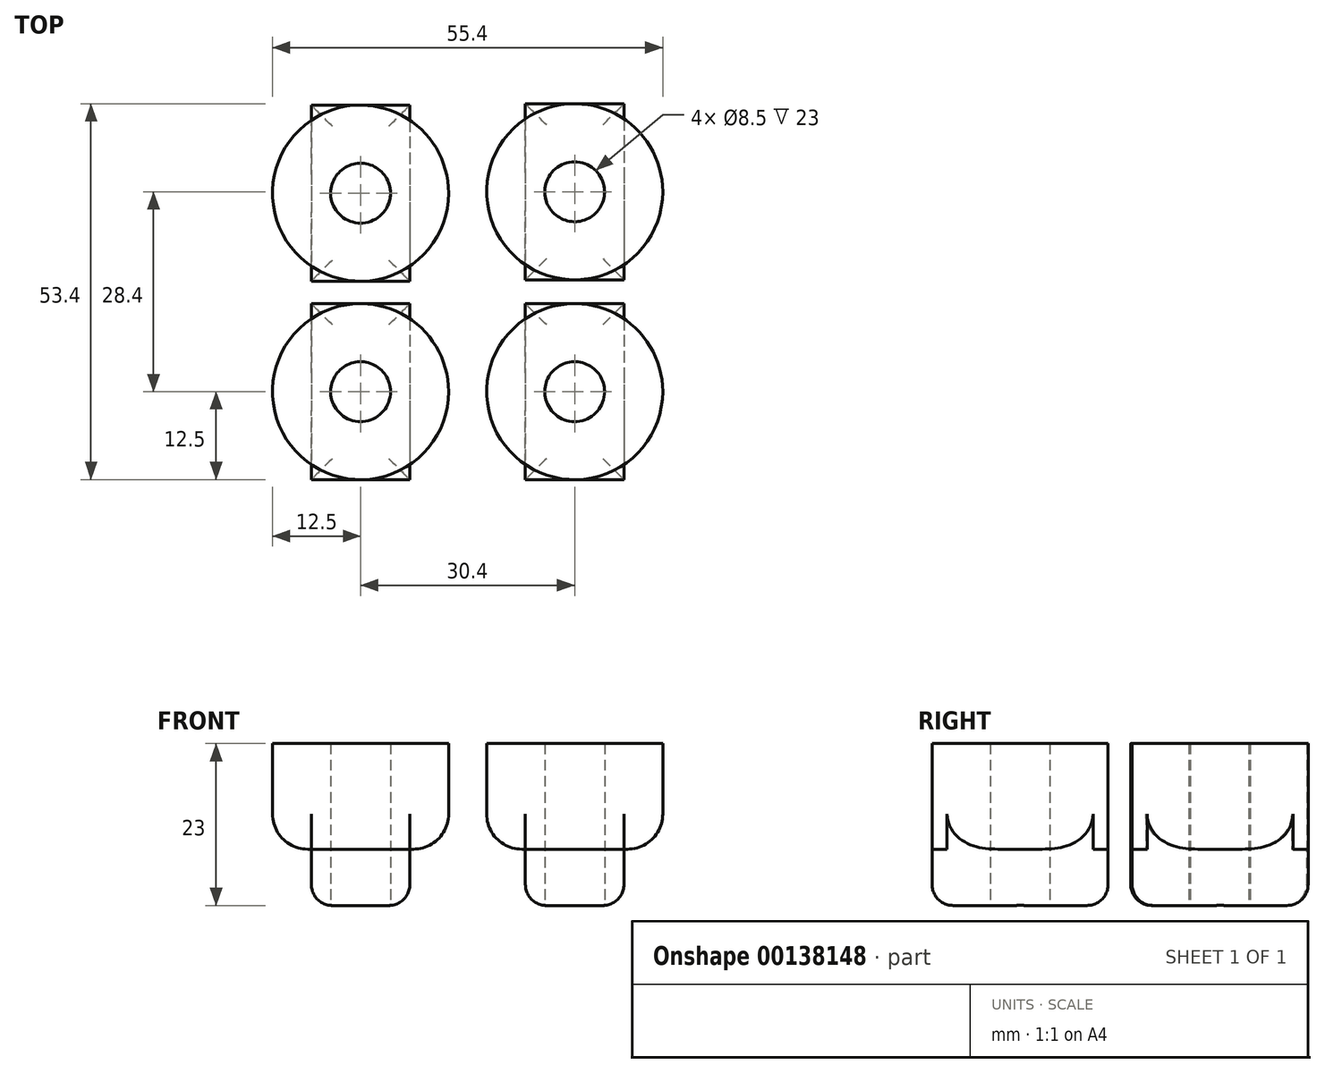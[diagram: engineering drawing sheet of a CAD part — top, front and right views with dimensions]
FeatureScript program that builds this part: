
annotation { "Feature Type Name" : "Feature", "Feature Type Description" : "" }
export const myFeature = defineFeature(function(context is Context, id is Id, definition is map)
    precondition{}
    {
        {
            var Q0;
            Q0=qCreatedBy(makeId("Top.planeOp"),FACE);
            var sketch = newSketch(context, id + "F0", { "sketchPlane" : qUnion([Q0])});
            skCircle(sketch, "E0", {"center": v(0, 0) * mm, "radius": 12.5 * mm});
            skCircle(sketch, "E1", {"center": v(0, 0) * mm, "radius": 4.25 * mm});
            skSolve(sketch);
        }
        {
            var Q0;
            Q0=makeQuery(id+"F0.imprint","IMPRINT",FACE,{"disambiguationData":[TD([[makeQuery(id+"F0.imprint","IMPRINT",EDGE,{"derivedFrom":sQuery(id+"F0.wireOp",EDGE,"E0")}),1.0]])]});
            extrude(context, id + "F1", {"entities" : qUnion([Q0]), "depth" : 15 * mm});
        }
        {
            var Q0;
            Q0=qCreatedBy(makeId("Top.planeOp"),FACE);
            var sketch = newSketch(context, id + "F2", { "sketchPlane" : qUnion([Q0])});
            skLineSegment(sketch, "E2.bottom", {"start": v(-7, 12.5) * mm, "end": v(7, 12.5) * mm});
            skLineSegment(sketch, "E2.top", {"start": v(-7, -12.5) * mm, "end": v(7, -12.5) * mm});
            skLineSegment(sketch, "E2.left", {"start": v(-7, 12.5) * mm, "end": v(-7, -12.5) * mm});
            skLineSegment(sketch, "E2.right", {"start": v(7, 12.5) * mm, "end": v(7, -12.5) * mm});
            skPoint(sketch, "E2.middle", {"position": v(0, 0) * mm});
            skSolve(sketch);
        }
        {
            var Q0;
            Q0=makeQuery(id+"F2.imprint","IMPRINT",FACE,{"disambiguationData":[TD([[makeQuery(id+"F2.imprint","IMPRINT",EDGE,{"derivedFrom":sQuery(id+"F2.wireOp",EDGE,"E2.bottom")}),-1.0]])]});
            extrude(context, id + "F3", {"entities" : qUnion([Q0]), "operationType" : NewBodyOperationType.ADD, "oppositeDirection" : true, "depth" : 8 * mm});
        }
        {
            var Q0;
            Q0=makeQuery(id+"F3.boolean.opBoolean","SPLIT",FACE,{"disambiguationData":[TD([makeQuery(id+"F1.opExtrude","SWEPT_FACE",FACE,{"disambiguationData":[OSD([sQuery(id+"F0.wireOp",EDGE,"E1")])]})])],"derivedFrom":makeQuery(id+"F3.opExtrude","CAP_FACE",FACE,{"disambiguationData":[OSD([sQuery(id+"F2.wireOp",EDGE,"E2.bottom"),sQuery(id+"F2.wireOp",EDGE,"E2.top"),sQuery(id+"F2.wireOp",EDGE,"E2.left"),sQuery(id+"F2.wireOp",EDGE,"E2.right")])],"isStart":true})});
            extrude(context, id + "F4", {"entities" : qUnion([Q0]), "operationType" : NewBodyOperationType.REMOVE, "oppositeDirection" : true, "depth" : 10 * mm});
        }
        {
            var Q0;
            Q0=makeQuery(id+"F3.opExtrude","CAP_EDGE",EDGE,{"disambiguationData":[OSD([sQuery(id+"F2.wireOp",EDGE,"E2.top")])],"isStart":false});
            var Q1;
            Q1=makeQuery(id+"F3.opExtrude","CAP_EDGE",EDGE,{"disambiguationData":[OSD([sQuery(id+"F2.wireOp",EDGE,"E2.right")])],"isStart":false});
            var Q2;
            Q2=makeQuery(id+"F3.opExtrude","CAP_EDGE",EDGE,{"disambiguationData":[OSD([sQuery(id+"F2.wireOp",EDGE,"E2.bottom")])],"isStart":false});
            var Q3;
            Q3=makeQuery(id+"F3.opExtrude","CAP_EDGE",EDGE,{"disambiguationData":[OSD([sQuery(id+"F2.wireOp",EDGE,"E2.left")])],"isStart":false});
            fillet(context, id + "F5", {"entities" : qUnion([Q0, Q1, Q2, Q3]), "radius" : 3 * mm, "tangentPropagation" : true, "allowEdgeOverflow" : false});
        }
        {
            var Q0;
            {var subQ0=sQuery(id+"F2.wireOp",EDGE,"E2.right");var subQ1=sQuery(id+"F2.wireOp",EDGE,"E2.bottom");var subQ2=makeQuery(id+"F3.opExtrude","CAP_FACE",FACE,{"disambiguationData":[OSD([subQ1,sQuery(id+"F2.wireOp",EDGE,"E2.top"),sQuery(id+"F2.wireOp",EDGE,"E2.left"),subQ0])],"isStart":true});var subQ3=sQuery(id+"F0.wireOp",EDGE,"E0");var subQ4=makeQuery(id+"F1.opExtrude","SWEPT_FACE",FACE,{"disambiguationData":[OSD([subQ3])]});Q0=makeQuery(id+"F3.boolean.opBoolean","SPLIT",EDGE,{"disambiguationData":[topologyDisambiguationEdgeConnected([subQ4,subQ2]),TD([subQ4,makeQuery(id+"F1.opExtrude","CAP_FACE",FACE,{"disambiguationData":[OSD([subQ3,sQuery(id+"F0.wireOp",EDGE,"E1")])],"isStart":true}),makeQuery(id+"F3.opExtrude","SWEPT_FACE",FACE,{"disambiguationData":[OSD([subQ1])]}),subQ2,makeQuery(id+"F3.opExtrude","SWEPT_FACE",FACE,{"disambiguationData":[OSD([subQ0])]})])],"derivedFrom":makeQuery(id+"F1.opExtrude","CAP_EDGE",EDGE,{"disambiguationData":[OSD([subQ3])],"isStart":true})});}
            var Q1;
            {var subQ0=sQuery(id+"F2.wireOp",EDGE,"E2.right");var subQ1=sQuery(id+"F2.wireOp",EDGE,"E2.top");var subQ2=makeQuery(id+"F3.opExtrude","CAP_FACE",FACE,{"disambiguationData":[OSD([sQuery(id+"F2.wireOp",EDGE,"E2.bottom"),subQ1,sQuery(id+"F2.wireOp",EDGE,"E2.left"),subQ0])],"isStart":true});var subQ3=sQuery(id+"F0.wireOp",EDGE,"E0");var subQ4=makeQuery(id+"F1.opExtrude","SWEPT_FACE",FACE,{"disambiguationData":[OSD([subQ3])]});Q1=makeQuery(id+"F3.boolean.opBoolean","SPLIT",EDGE,{"disambiguationData":[topologyDisambiguationEdgeConnected([subQ4,subQ2]),TD([subQ4,makeQuery(id+"F1.opExtrude","CAP_FACE",FACE,{"disambiguationData":[OSD([subQ3,sQuery(id+"F0.wireOp",EDGE,"E1")])],"isStart":true}),subQ2,makeQuery(id+"F3.opExtrude","SWEPT_FACE",FACE,{"disambiguationData":[OSD([subQ1])]}),makeQuery(id+"F3.opExtrude","SWEPT_FACE",FACE,{"disambiguationData":[OSD([subQ0])]})])],"derivedFrom":makeQuery(id+"F1.opExtrude","CAP_EDGE",EDGE,{"disambiguationData":[OSD([subQ3])],"isStart":true})});}
            fillet(context, id + "F6", {"entities" : qUnion([Q0, Q1]), "radius" : 5 * mm, "tangentPropagation" : true, "allowEdgeOverflow" : false});
        }
        {
            var Q0;
            Q0=makeQuery(id+"F1.opExtrude","SWEPT_BODY",BODY,{"disambiguationData":[OSD([sQuery(id+"F0.wireOp",EDGE,"E0"),sQuery(id+"F0.wireOp",EDGE,"E1")])]});
            transform(context, id + "F7", {"entities" : qUnion([Q0]), "transformType" : TransformType.TRANSLATION_3D, "dx" : -30.4 * mm, "dy" : 0 * mm, "dz" : 0 * mm, "makeCopy" : true});
        }
        {
            var Q0;
            Q0=makeQuery(id+"F1.opExtrude","SWEPT_BODY",BODY,{"disambiguationData":[OSD([sQuery(id+"F0.wireOp",EDGE,"E0"),sQuery(id+"F0.wireOp",EDGE,"E1")])]});
            transform(context, id + "F8", {"entities" : qUnion([Q0]), "transformType" : TransformType.TRANSLATION_3D, "dx" : -30.4 * mm, "dy" : 28.2 * mm, "dz" : 0 * mm, "makeCopy" : true});
        }
        {
            var Q0;
            Q0=makeQuery(id+"F1.opExtrude","SWEPT_BODY",BODY,{"disambiguationData":[OSD([sQuery(id+"F0.wireOp",EDGE,"E0"),sQuery(id+"F0.wireOp",EDGE,"E1")])]});
            transform(context, id + "F9", {"entities" : qUnion([Q0]), "transformType" : TransformType.TRANSLATION_3D, "dx" : 0 * mm, "dy" : 28.4 * mm, "dz" : 0 * mm, "makeCopy" : true});
        }
    });
